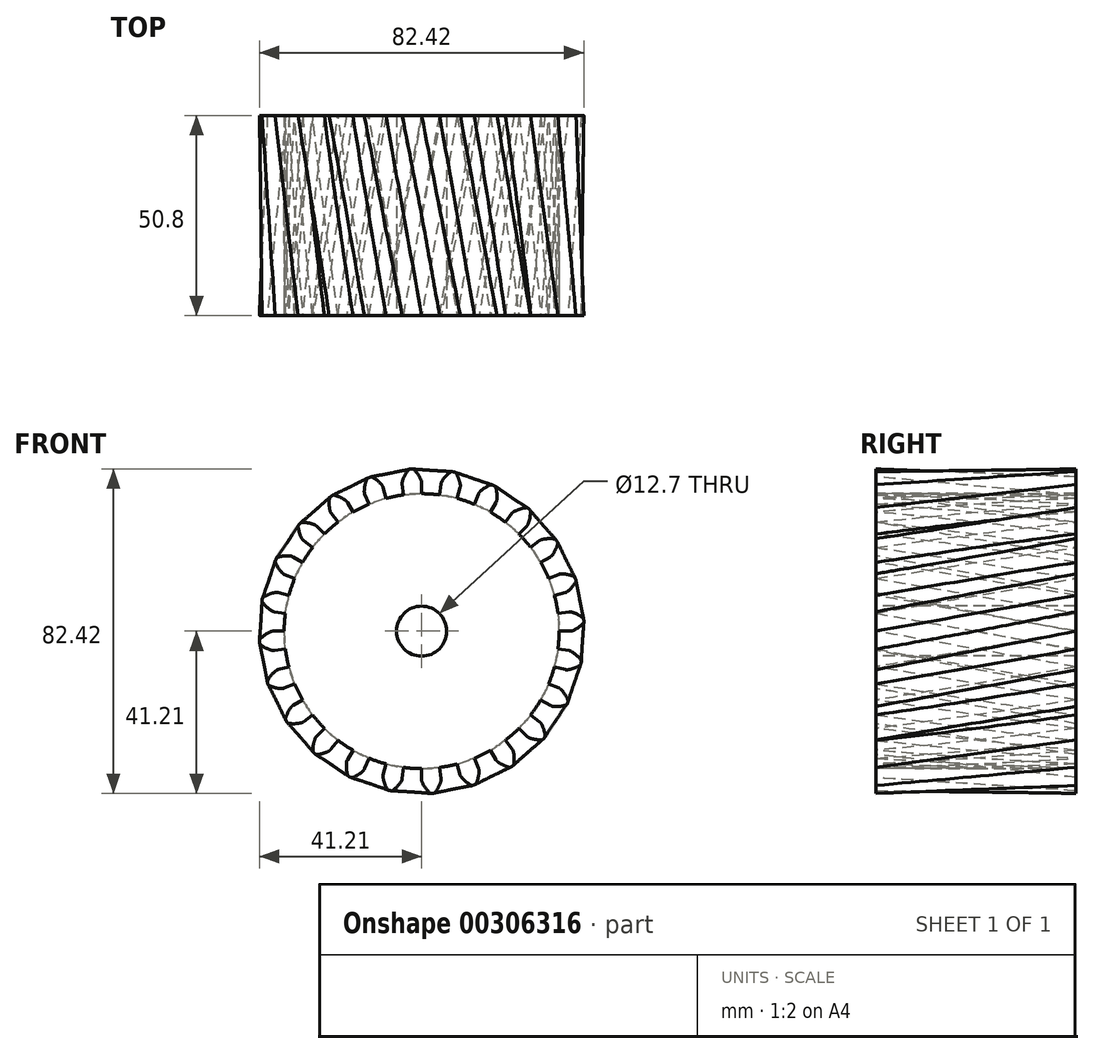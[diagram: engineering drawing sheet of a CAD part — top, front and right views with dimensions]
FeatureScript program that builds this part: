
annotation { "Feature Type Name" : "Feature", "Feature Type Description" : "" }
export const myFeature = defineFeature(function(context is Context, id is Id, definition is map)
    precondition{}
    {
        {
            var Q0;
            Q0=qCreatedBy(makeId("Front.planeOp"),FACE);
            var sketch = newSketch(context, id + "F0", { "sketchPlane" : qUnion([Q0])});
            skCircle(sketch, "E0", {"center": v(0, 0) * mm, "radius": 34.93 * mm});
            skArc(sketch, "E1.trimOffspring", {"start": v(-0.14, 38.43) * mm, "mid": v(-0.94, 39.83) * mm, "end": v(-1.99, 41.06) * mm});
            skLineSegment(sketch, "E2", {"start": v(0, 37.78) * mm, "end": v(0, 34.93) * mm});
            skLineSegment(sketch, "E3", {"start": v(-2.37, 41.2) * mm, "end": v(-2.7, 41.2) * mm});
            skArc(sketch, "E4.MirrorCS", {"start": v(-4.88, 38.12) * mm, "mid": v(-4.27, 39.62) * mm, "end": v(-3.4, 40.97) * mm});
            skLineSegment(sketch, "E5.MirrorCS", {"start": v(-3.03, 41.16) * mm, "end": v(-2.7, 41.2) * mm});
            skLineSegment(sketch, "E6.MirrorCS", {"start": v(-4.93, 37.45) * mm, "end": v(-4.56, 34.63) * mm});
            skPoint(sketch, "E7.visualSharp", {"position": v(-4.97, 37.77) * mm});
            skArc(sketch, "E7.filletArc", {"start": v(-4.88, 38.12) * mm, "mid": v(-4.94, 37.79) * mm, "end": v(-4.93, 37.45) * mm});
            skPoint(sketch, "E8.visualSharp", {"position": v(0, 38.1) * mm});
            skArc(sketch, "E8.filletArc", {"start": v(0, 37.78) * mm, "mid": v(-0.04, 38.11) * mm, "end": v(-0.14, 38.43) * mm});
            skPoint(sketch, "E9.visualSharp", {"position": v(-3.25, 41.15) * mm});
            skArc(sketch, "E9.filletArc", {"start": v(-3.03, 41.16) * mm, "mid": v(-3.23, 41.1) * mm, "end": v(-3.4, 40.97) * mm});
            skPoint(sketch, "E10.visualSharp", {"position": v(-2.15, 41.22) * mm});
            skArc(sketch, "E10.filletArc", {"start": v(-1.99, 41.06) * mm, "mid": v(-2.16, 41.18) * mm, "end": v(-2.37, 41.2) * mm});
            skLineSegment(sketch, "E11.1.0", {"start": v(-14.46, 34.9) * mm, "end": v(-13.37, 32.27) * mm});
            skArc(sketch, "E11.1.1", {"start": v(-14.58, 35.56) * mm, "mid": v(-14.55, 35.22) * mm, "end": v(-14.46, 34.9) * mm});
            skArc(sketch, "E11.1.2", {"start": v(-14.58, 35.56) * mm, "mid": v(-14.38, 37.16) * mm, "end": v(-13.88, 38.7) * mm});
            skLineSegment(sketch, "E11.1.3", {"start": v(-13.58, 38.98) * mm, "end": v(-13.27, 39.09) * mm});
            skLineSegment(sketch, "E11.1.4", {"start": v(-12.95, 39.2) * mm, "end": v(-13.27, 39.09) * mm});
            skArc(sketch, "E11.1.5", {"start": v(-10.08, 37.08) * mm, "mid": v(-11.22, 38.23) * mm, "end": v(-12.55, 39.15) * mm});
            skArc(sketch, "E11.1.6", {"start": v(-9.78, 36.5) * mm, "mid": v(-9.9, 36.8) * mm, "end": v(-10.08, 37.08) * mm});
            skLineSegment(sketch, "E11.1.7", {"start": v(-9.78, 36.5) * mm, "end": v(-9.04, 33.73) * mm});
            skArc(sketch, "E11.1.8", {"start": v(-13.58, 38.98) * mm, "mid": v(-13.76, 38.87) * mm, "end": v(-13.88, 38.7) * mm});
            skArc(sketch, "E11.1.9", {"start": v(-12.55, 39.15) * mm, "mid": v(-12.74, 39.21) * mm, "end": v(-12.95, 39.2) * mm});
            skLineSegment(sketch, "E11.2.0", {"start": v(-23, 29.97) * mm, "end": v(-21.26, 27.7) * mm});
            skArc(sketch, "E11.2.1", {"start": v(-23.28, 30.57) * mm, "mid": v(-23.17, 30.26) * mm, "end": v(-23, 29.97) * mm});
            skArc(sketch, "E11.2.2", {"start": v(-23.28, 30.57) * mm, "mid": v(-23.5, 32.17) * mm, "end": v(-23.42, 33.79) * mm});
            skLineSegment(sketch, "E11.2.3", {"start": v(-23.2, 34.13) * mm, "end": v(-22.93, 34.32) * mm});
            skLineSegment(sketch, "E11.2.4", {"start": v(-22.65, 34.5) * mm, "end": v(-22.93, 34.32) * mm});
            skArc(sketch, "E11.2.5", {"start": v(-19.34, 33.21) * mm, "mid": v(-20.73, 34.03) * mm, "end": v(-22.25, 34.57) * mm});
            skArc(sketch, "E11.2.6", {"start": v(-18.89, 32.72) * mm, "mid": v(-19.09, 32.99) * mm, "end": v(-19.34, 33.21) * mm});
            skLineSegment(sketch, "E11.2.7", {"start": v(-18.89, 32.72) * mm, "end": v(-17.46, 30.25) * mm});
            skArc(sketch, "E11.2.8", {"start": v(-23.2, 34.13) * mm, "mid": v(-23.35, 33.98) * mm, "end": v(-23.42, 33.79) * mm});
            skArc(sketch, "E11.2.9", {"start": v(-22.25, 34.57) * mm, "mid": v(-22.46, 34.58) * mm, "end": v(-22.65, 34.5) * mm});
            skLineSegment(sketch, "E12.2.3.0", {"start": v(-29.97, 23) * mm, "end": v(-27.7, 21.26) * mm});
            skArc(sketch, "E12.3.3.0", {"start": v(-30.4, 23.5) * mm, "mid": v(-30.21, 23.23) * mm, "end": v(-29.97, 23) * mm});
            skArc(sketch, "E12.7.3.0", {"start": v(-30.4, 23.5) * mm, "mid": v(-31.03, 25) * mm, "end": v(-31.37, 26.57) * mm});
            skLineSegment(sketch, "E12.11.3.0", {"start": v(-31.25, 26.96) * mm, "end": v(-31.03, 27.22) * mm});
            skLineSegment(sketch, "E12.14.3.0", {"start": v(-30.81, 27.47) * mm, "end": v(-31.03, 27.22) * mm});
            skArc(sketch, "E12.17.3.0", {"start": v(-27.27, 27.07) * mm, "mid": v(-28.83, 27.5) * mm, "end": v(-30.44, 27.63) * mm});
            skArc(sketch, "E12.21.3.0", {"start": v(-26.71, 26.71) * mm, "mid": v(-26.97, 26.92) * mm, "end": v(-27.27, 27.07) * mm});
            skLineSegment(sketch, "E12.25.3.0", {"start": v(-26.71, 26.71) * mm, "end": v(-24.7, 24.7) * mm});
            skArc(sketch, "E12.28.3.0", {"start": v(-31.25, 26.96) * mm, "mid": v(-31.35, 26.78) * mm, "end": v(-31.37, 26.57) * mm});
            skArc(sketch, "E12.32.3.0", {"start": v(-30.44, 27.63) * mm, "mid": v(-30.64, 27.59) * mm, "end": v(-30.81, 27.47) * mm});
            skLineSegment(sketch, "E12.2.4.0", {"start": v(-34.9, 14.46) * mm, "end": v(-32.27, 13.37) * mm});
            skArc(sketch, "E12.3.4.0", {"start": v(-35.45, 14.84) * mm, "mid": v(-35.2, 14.62) * mm, "end": v(-34.9, 14.46) * mm});
            skArc(sketch, "E12.7.4.0", {"start": v(-35.45, 14.84) * mm, "mid": v(-36.44, 16.11) * mm, "end": v(-37.18, 17.55) * mm});
            skLineSegment(sketch, "E12.11.4.0", {"start": v(-37.17, 17.96) * mm, "end": v(-37.02, 18.26) * mm});
            skLineSegment(sketch, "E12.14.4.0", {"start": v(-36.87, 18.55) * mm, "end": v(-37.02, 18.26) * mm});
            skArc(sketch, "E12.17.4.0", {"start": v(-33.35, 19.1) * mm, "mid": v(-34.97, 19.1) * mm, "end": v(-36.56, 18.81) * mm});
            skArc(sketch, "E12.21.4.0", {"start": v(-32.72, 18.89) * mm, "mid": v(-33.02, 19.02) * mm, "end": v(-33.35, 19.1) * mm});
            skLineSegment(sketch, "E12.25.4.0", {"start": v(-32.72, 18.89) * mm, "end": v(-30.25, 17.46) * mm});
            skArc(sketch, "E12.28.4.0", {"start": v(-37.17, 17.96) * mm, "mid": v(-37.21, 17.75) * mm, "end": v(-37.18, 17.55) * mm});
            skArc(sketch, "E12.32.4.0", {"start": v(-36.56, 18.81) * mm, "mid": v(-36.74, 18.72) * mm, "end": v(-36.87, 18.55) * mm});
            skLineSegment(sketch, "E12.2.5.0", {"start": v(-37.45, 4.93) * mm, "end": v(-34.63, 4.56) * mm});
            skArc(sketch, "E12.3.5.0", {"start": v(-38.08, 5.15) * mm, "mid": v(-37.78, 5) * mm, "end": v(-37.45, 4.93) * mm});
            skArc(sketch, "E12.7.5.0", {"start": v(-38.08, 5.15) * mm, "mid": v(-39.37, 6.13) * mm, "end": v(-40.45, 7.33) * mm});
            skLineSegment(sketch, "E12.11.5.0", {"start": v(-40.55, 7.72) * mm, "end": v(-40.49, 8.05) * mm});
            skLineSegment(sketch, "E12.14.5.0", {"start": v(-40.42, 8.38) * mm, "end": v(-40.49, 8.05) * mm});
            skArc(sketch, "E12.17.5.0", {"start": v(-37.16, 9.81) * mm, "mid": v(-38.72, 9.4) * mm, "end": v(-40.18, 8.71) * mm});
            skArc(sketch, "E12.21.5.0", {"start": v(-36.5, 9.78) * mm, "mid": v(-36.82, 9.83) * mm, "end": v(-37.16, 9.81) * mm});
            skLineSegment(sketch, "E12.25.5.0", {"start": v(-36.5, 9.78) * mm, "end": v(-33.73, 9.04) * mm});
            skArc(sketch, "E12.28.5.0", {"start": v(-40.55, 7.72) * mm, "mid": v(-40.54, 7.52) * mm, "end": v(-40.45, 7.33) * mm});
            skArc(sketch, "E12.32.5.0", {"start": v(-40.18, 8.71) * mm, "mid": v(-40.33, 8.57) * mm, "end": v(-40.42, 8.38) * mm});
            skLineSegment(sketch, "E12.2.6.0", {"start": v(-37.45, -4.93) * mm, "end": v(-34.63, -4.56) * mm});
            skArc(sketch, "E12.3.6.0", {"start": v(-38.12, -4.88) * mm, "mid": v(-37.79, -4.94) * mm, "end": v(-37.45, -4.93) * mm});
            skArc(sketch, "E12.7.6.0", {"start": v(-38.12, -4.88) * mm, "mid": v(-39.62, -4.27) * mm, "end": v(-40.97, -3.4) * mm});
            skLineSegment(sketch, "E12.11.6.0", {"start": v(-41.16, -3.03) * mm, "end": v(-41.2, -2.7) * mm});
            skLineSegment(sketch, "E12.14.6.0", {"start": v(-41.2, -2.37) * mm, "end": v(-41.2, -2.7) * mm});
            skArc(sketch, "E12.17.6.0", {"start": v(-38.43, -0.14) * mm, "mid": v(-39.83, -0.94) * mm, "end": v(-41.06, -1.99) * mm});
            skArc(sketch, "E12.21.6.0", {"start": v(-37.78, 0) * mm, "mid": v(-38.11, -0.04) * mm, "end": v(-38.43, -0.14) * mm});
            skLineSegment(sketch, "E12.25.6.0", {"start": v(-37.78, 0) * mm, "end": v(-34.93, 0) * mm});
            skArc(sketch, "E12.28.6.0", {"start": v(-41.16, -3.03) * mm, "mid": v(-41.1, -3.23) * mm, "end": v(-40.97, -3.4) * mm});
            skArc(sketch, "E12.32.6.0", {"start": v(-41.06, -1.99) * mm, "mid": v(-41.18, -2.16) * mm, "end": v(-41.2, -2.37) * mm});
            skLineSegment(sketch, "E12.2.7.0", {"start": v(-34.9, -14.46) * mm, "end": v(-32.27, -13.37) * mm});
            skArc(sketch, "E12.3.7.0", {"start": v(-35.56, -14.58) * mm, "mid": v(-35.22, -14.55) * mm, "end": v(-34.9, -14.46) * mm});
            skArc(sketch, "E12.7.7.0", {"start": v(-35.56, -14.58) * mm, "mid": v(-37.16, -14.38) * mm, "end": v(-38.7, -13.88) * mm});
            skLineSegment(sketch, "E12.11.7.0", {"start": v(-38.98, -13.58) * mm, "end": v(-39.09, -13.27) * mm});
            skLineSegment(sketch, "E12.14.7.0", {"start": v(-39.2, -12.95) * mm, "end": v(-39.09, -13.27) * mm});
            skArc(sketch, "E12.17.7.0", {"start": v(-37.08, -10.08) * mm, "mid": v(-38.23, -11.22) * mm, "end": v(-39.15, -12.55) * mm});
            skArc(sketch, "E12.21.7.0", {"start": v(-36.5, -9.78) * mm, "mid": v(-36.8, -9.9) * mm, "end": v(-37.08, -10.08) * mm});
            skLineSegment(sketch, "E12.25.7.0", {"start": v(-36.5, -9.78) * mm, "end": v(-33.73, -9.04) * mm});
            skArc(sketch, "E12.28.7.0", {"start": v(-38.98, -13.58) * mm, "mid": v(-38.87, -13.76) * mm, "end": v(-38.7, -13.88) * mm});
            skArc(sketch, "E12.32.7.0", {"start": v(-39.15, -12.55) * mm, "mid": v(-39.21, -12.74) * mm, "end": v(-39.2, -12.95) * mm});
            skLineSegment(sketch, "E12.2.8.0", {"start": v(-29.97, -23) * mm, "end": v(-27.7, -21.26) * mm});
            skArc(sketch, "E12.3.8.0", {"start": v(-30.57, -23.28) * mm, "mid": v(-30.26, -23.17) * mm, "end": v(-29.97, -23) * mm});
            skArc(sketch, "E12.7.8.0", {"start": v(-30.57, -23.28) * mm, "mid": v(-32.17, -23.5) * mm, "end": v(-33.79, -23.42) * mm});
            skLineSegment(sketch, "E12.11.8.0", {"start": v(-34.13, -23.2) * mm, "end": v(-34.32, -22.93) * mm});
            skLineSegment(sketch, "E12.14.8.0", {"start": v(-34.5, -22.65) * mm, "end": v(-34.32, -22.93) * mm});
            skArc(sketch, "E12.17.8.0", {"start": v(-33.21, -19.34) * mm, "mid": v(-34.03, -20.73) * mm, "end": v(-34.57, -22.25) * mm});
            skArc(sketch, "E12.21.8.0", {"start": v(-32.72, -18.89) * mm, "mid": v(-32.99, -19.09) * mm, "end": v(-33.21, -19.34) * mm});
            skLineSegment(sketch, "E12.25.8.0", {"start": v(-32.72, -18.89) * mm, "end": v(-30.25, -17.46) * mm});
            skArc(sketch, "E12.28.8.0", {"start": v(-34.13, -23.2) * mm, "mid": v(-33.98, -23.35) * mm, "end": v(-33.79, -23.42) * mm});
            skArc(sketch, "E12.32.8.0", {"start": v(-34.57, -22.25) * mm, "mid": v(-34.58, -22.46) * mm, "end": v(-34.5, -22.65) * mm});
            skLineSegment(sketch, "E12.2.9.0", {"start": v(-23, -29.97) * mm, "end": v(-21.26, -27.7) * mm});
            skArc(sketch, "E12.3.9.0", {"start": v(-23.5, -30.4) * mm, "mid": v(-23.23, -30.21) * mm, "end": v(-23, -29.97) * mm});
            skArc(sketch, "E12.7.9.0", {"start": v(-23.5, -30.4) * mm, "mid": v(-25, -31.03) * mm, "end": v(-26.57, -31.37) * mm});
            skLineSegment(sketch, "E12.11.9.0", {"start": v(-26.96, -31.25) * mm, "end": v(-27.22, -31.03) * mm});
            skLineSegment(sketch, "E12.14.9.0", {"start": v(-27.47, -30.81) * mm, "end": v(-27.22, -31.03) * mm});
            skArc(sketch, "E12.17.9.0", {"start": v(-27.07, -27.27) * mm, "mid": v(-27.5, -28.83) * mm, "end": v(-27.63, -30.44) * mm});
            skArc(sketch, "E12.21.9.0", {"start": v(-26.71, -26.71) * mm, "mid": v(-26.92, -26.97) * mm, "end": v(-27.07, -27.27) * mm});
            skLineSegment(sketch, "E12.25.9.0", {"start": v(-26.71, -26.71) * mm, "end": v(-24.7, -24.7) * mm});
            skArc(sketch, "E12.28.9.0", {"start": v(-26.96, -31.25) * mm, "mid": v(-26.78, -31.35) * mm, "end": v(-26.57, -31.37) * mm});
            skArc(sketch, "E12.32.9.0", {"start": v(-27.63, -30.44) * mm, "mid": v(-27.59, -30.64) * mm, "end": v(-27.47, -30.81) * mm});
            skLineSegment(sketch, "E12.2.10.0", {"start": v(-14.46, -34.9) * mm, "end": v(-13.37, -32.27) * mm});
            skArc(sketch, "E12.3.10.0", {"start": v(-14.84, -35.45) * mm, "mid": v(-14.62, -35.2) * mm, "end": v(-14.46, -34.9) * mm});
            skArc(sketch, "E12.7.10.0", {"start": v(-14.84, -35.45) * mm, "mid": v(-16.11, -36.44) * mm, "end": v(-17.55, -37.18) * mm});
            skLineSegment(sketch, "E12.11.10.0", {"start": v(-17.96, -37.17) * mm, "end": v(-18.26, -37.02) * mm});
            skLineSegment(sketch, "E12.14.10.0", {"start": v(-18.55, -36.87) * mm, "end": v(-18.26, -37.02) * mm});
            skArc(sketch, "E12.17.10.0", {"start": v(-19.1, -33.35) * mm, "mid": v(-19.1, -34.97) * mm, "end": v(-18.81, -36.56) * mm});
            skArc(sketch, "E12.21.10.0", {"start": v(-18.89, -32.72) * mm, "mid": v(-19.02, -33.02) * mm, "end": v(-19.1, -33.35) * mm});
            skLineSegment(sketch, "E12.25.10.0", {"start": v(-18.89, -32.72) * mm, "end": v(-17.46, -30.25) * mm});
            skArc(sketch, "E12.28.10.0", {"start": v(-17.96, -37.17) * mm, "mid": v(-17.75, -37.21) * mm, "end": v(-17.55, -37.18) * mm});
            skArc(sketch, "E12.32.10.0", {"start": v(-18.81, -36.56) * mm, "mid": v(-18.72, -36.74) * mm, "end": v(-18.55, -36.87) * mm});
            skLineSegment(sketch, "E12.2.11.0", {"start": v(-4.93, -37.45) * mm, "end": v(-4.56, -34.63) * mm});
            skArc(sketch, "E12.3.11.0", {"start": v(-5.15, -38.08) * mm, "mid": v(-5, -37.78) * mm, "end": v(-4.93, -37.45) * mm});
            skArc(sketch, "E12.7.11.0", {"start": v(-5.15, -38.08) * mm, "mid": v(-6.13, -39.37) * mm, "end": v(-7.33, -40.45) * mm});
            skLineSegment(sketch, "E12.11.11.0", {"start": v(-7.72, -40.55) * mm, "end": v(-8.05, -40.49) * mm});
            skLineSegment(sketch, "E12.14.11.0", {"start": v(-8.38, -40.42) * mm, "end": v(-8.05, -40.49) * mm});
            skArc(sketch, "E12.17.11.0", {"start": v(-9.81, -37.16) * mm, "mid": v(-9.4, -38.72) * mm, "end": v(-8.71, -40.18) * mm});
            skArc(sketch, "E12.21.11.0", {"start": v(-9.78, -36.5) * mm, "mid": v(-9.83, -36.82) * mm, "end": v(-9.81, -37.16) * mm});
            skLineSegment(sketch, "E12.25.11.0", {"start": v(-9.78, -36.5) * mm, "end": v(-9.04, -33.73) * mm});
            skArc(sketch, "E12.28.11.0", {"start": v(-7.72, -40.55) * mm, "mid": v(-7.52, -40.54) * mm, "end": v(-7.33, -40.45) * mm});
            skArc(sketch, "E12.32.11.0", {"start": v(-8.71, -40.18) * mm, "mid": v(-8.57, -40.33) * mm, "end": v(-8.38, -40.42) * mm});
            skLineSegment(sketch, "E12.2.12.0", {"start": v(4.93, -37.45) * mm, "end": v(4.56, -34.63) * mm});
            skArc(sketch, "E12.3.12.0", {"start": v(4.88, -38.12) * mm, "mid": v(4.94, -37.79) * mm, "end": v(4.93, -37.45) * mm});
            skArc(sketch, "E12.7.12.0", {"start": v(4.88, -38.12) * mm, "mid": v(4.27, -39.62) * mm, "end": v(3.4, -40.97) * mm});
            skLineSegment(sketch, "E12.11.12.0", {"start": v(3.03, -41.16) * mm, "end": v(2.7, -41.2) * mm});
            skLineSegment(sketch, "E12.14.12.0", {"start": v(2.37, -41.2) * mm, "end": v(2.7, -41.2) * mm});
            skArc(sketch, "E12.17.12.0", {"start": v(0.14, -38.43) * mm, "mid": v(0.94, -39.83) * mm, "end": v(1.99, -41.06) * mm});
            skArc(sketch, "E12.21.12.0", {"start": v(0, -37.78) * mm, "mid": v(0.04, -38.11) * mm, "end": v(0.14, -38.43) * mm});
            skLineSegment(sketch, "E12.25.12.0", {"start": v(0, -37.78) * mm, "end": v(0, -34.93) * mm});
            skArc(sketch, "E12.28.12.0", {"start": v(3.03, -41.16) * mm, "mid": v(3.23, -41.1) * mm, "end": v(3.4, -40.97) * mm});
            skArc(sketch, "E12.32.12.0", {"start": v(1.99, -41.06) * mm, "mid": v(2.16, -41.18) * mm, "end": v(2.37, -41.2) * mm});
            skLineSegment(sketch, "E12.2.13.0", {"start": v(14.46, -34.9) * mm, "end": v(13.37, -32.27) * mm});
            skArc(sketch, "E12.3.13.0", {"start": v(14.58, -35.56) * mm, "mid": v(14.55, -35.22) * mm, "end": v(14.46, -34.9) * mm});
            skArc(sketch, "E12.7.13.0", {"start": v(14.58, -35.56) * mm, "mid": v(14.38, -37.16) * mm, "end": v(13.88, -38.7) * mm});
            skLineSegment(sketch, "E12.11.13.0", {"start": v(13.58, -38.98) * mm, "end": v(13.27, -39.09) * mm});
            skLineSegment(sketch, "E12.14.13.0", {"start": v(12.95, -39.2) * mm, "end": v(13.27, -39.09) * mm});
            skArc(sketch, "E12.17.13.0", {"start": v(10.08, -37.08) * mm, "mid": v(11.22, -38.23) * mm, "end": v(12.55, -39.15) * mm});
            skArc(sketch, "E12.21.13.0", {"start": v(9.78, -36.5) * mm, "mid": v(9.9, -36.8) * mm, "end": v(10.08, -37.08) * mm});
            skLineSegment(sketch, "E12.25.13.0", {"start": v(9.78, -36.5) * mm, "end": v(9.04, -33.73) * mm});
            skArc(sketch, "E12.28.13.0", {"start": v(13.58, -38.98) * mm, "mid": v(13.76, -38.87) * mm, "end": v(13.88, -38.7) * mm});
            skArc(sketch, "E12.32.13.0", {"start": v(12.55, -39.15) * mm, "mid": v(12.74, -39.21) * mm, "end": v(12.95, -39.2) * mm});
            skLineSegment(sketch, "E12.2.14.0", {"start": v(23, -29.97) * mm, "end": v(21.26, -27.7) * mm});
            skArc(sketch, "E12.3.14.0", {"start": v(23.28, -30.57) * mm, "mid": v(23.17, -30.26) * mm, "end": v(23, -29.97) * mm});
            skArc(sketch, "E12.7.14.0", {"start": v(23.28, -30.57) * mm, "mid": v(23.5, -32.17) * mm, "end": v(23.42, -33.79) * mm});
            skLineSegment(sketch, "E12.11.14.0", {"start": v(23.2, -34.13) * mm, "end": v(22.93, -34.32) * mm});
            skLineSegment(sketch, "E12.14.14.0", {"start": v(22.65, -34.5) * mm, "end": v(22.93, -34.32) * mm});
            skArc(sketch, "E12.17.14.0", {"start": v(19.34, -33.21) * mm, "mid": v(20.73, -34.03) * mm, "end": v(22.25, -34.57) * mm});
            skArc(sketch, "E12.21.14.0", {"start": v(18.89, -32.72) * mm, "mid": v(19.09, -32.99) * mm, "end": v(19.34, -33.21) * mm});
            skLineSegment(sketch, "E12.25.14.0", {"start": v(18.89, -32.72) * mm, "end": v(17.46, -30.25) * mm});
            skArc(sketch, "E12.28.14.0", {"start": v(23.2, -34.13) * mm, "mid": v(23.35, -33.98) * mm, "end": v(23.42, -33.79) * mm});
            skArc(sketch, "E12.32.14.0", {"start": v(22.25, -34.57) * mm, "mid": v(22.46, -34.58) * mm, "end": v(22.65, -34.5) * mm});
            skLineSegment(sketch, "E12.2.15.0", {"start": v(29.97, -23) * mm, "end": v(27.7, -21.26) * mm});
            skArc(sketch, "E12.3.15.0", {"start": v(30.4, -23.5) * mm, "mid": v(30.21, -23.23) * mm, "end": v(29.97, -23) * mm});
            skArc(sketch, "E12.7.15.0", {"start": v(30.4, -23.5) * mm, "mid": v(31.03, -25) * mm, "end": v(31.37, -26.57) * mm});
            skLineSegment(sketch, "E12.11.15.0", {"start": v(31.25, -26.96) * mm, "end": v(31.03, -27.22) * mm});
            skLineSegment(sketch, "E12.14.15.0", {"start": v(30.81, -27.47) * mm, "end": v(31.03, -27.22) * mm});
            skArc(sketch, "E12.17.15.0", {"start": v(27.27, -27.07) * mm, "mid": v(28.83, -27.5) * mm, "end": v(30.44, -27.63) * mm});
            skArc(sketch, "E12.21.15.0", {"start": v(26.71, -26.71) * mm, "mid": v(26.97, -26.92) * mm, "end": v(27.27, -27.07) * mm});
            skLineSegment(sketch, "E12.25.15.0", {"start": v(26.71, -26.71) * mm, "end": v(24.7, -24.7) * mm});
            skArc(sketch, "E12.28.15.0", {"start": v(31.25, -26.96) * mm, "mid": v(31.35, -26.78) * mm, "end": v(31.37, -26.57) * mm});
            skArc(sketch, "E12.32.15.0", {"start": v(30.44, -27.63) * mm, "mid": v(30.64, -27.59) * mm, "end": v(30.81, -27.47) * mm});
            skLineSegment(sketch, "E12.2.16.0", {"start": v(34.9, -14.46) * mm, "end": v(32.27, -13.37) * mm});
            skArc(sketch, "E12.3.16.0", {"start": v(35.45, -14.84) * mm, "mid": v(35.2, -14.62) * mm, "end": v(34.9, -14.46) * mm});
            skArc(sketch, "E12.7.16.0", {"start": v(35.45, -14.84) * mm, "mid": v(36.44, -16.11) * mm, "end": v(37.18, -17.55) * mm});
            skLineSegment(sketch, "E12.11.16.0", {"start": v(37.17, -17.96) * mm, "end": v(37.02, -18.26) * mm});
            skLineSegment(sketch, "E12.14.16.0", {"start": v(36.87, -18.55) * mm, "end": v(37.02, -18.26) * mm});
            skArc(sketch, "E12.17.16.0", {"start": v(33.35, -19.1) * mm, "mid": v(34.97, -19.1) * mm, "end": v(36.56, -18.81) * mm});
            skArc(sketch, "E12.21.16.0", {"start": v(32.72, -18.89) * mm, "mid": v(33.02, -19.02) * mm, "end": v(33.35, -19.1) * mm});
            skLineSegment(sketch, "E12.25.16.0", {"start": v(32.72, -18.89) * mm, "end": v(30.25, -17.46) * mm});
            skArc(sketch, "E12.28.16.0", {"start": v(37.17, -17.96) * mm, "mid": v(37.21, -17.75) * mm, "end": v(37.18, -17.55) * mm});
            skArc(sketch, "E12.32.16.0", {"start": v(36.56, -18.81) * mm, "mid": v(36.74, -18.72) * mm, "end": v(36.87, -18.55) * mm});
            skLineSegment(sketch, "E12.2.17.0", {"start": v(37.45, -4.93) * mm, "end": v(34.63, -4.56) * mm});
            skArc(sketch, "E12.3.17.0", {"start": v(38.08, -5.15) * mm, "mid": v(37.78, -5) * mm, "end": v(37.45, -4.93) * mm});
            skArc(sketch, "E12.7.17.0", {"start": v(38.08, -5.15) * mm, "mid": v(39.37, -6.13) * mm, "end": v(40.45, -7.33) * mm});
            skLineSegment(sketch, "E12.11.17.0", {"start": v(40.55, -7.72) * mm, "end": v(40.49, -8.05) * mm});
            skLineSegment(sketch, "E12.14.17.0", {"start": v(40.42, -8.38) * mm, "end": v(40.49, -8.05) * mm});
            skArc(sketch, "E12.17.17.0", {"start": v(37.16, -9.81) * mm, "mid": v(38.72, -9.4) * mm, "end": v(40.18, -8.71) * mm});
            skArc(sketch, "E12.21.17.0", {"start": v(36.5, -9.78) * mm, "mid": v(36.82, -9.83) * mm, "end": v(37.16, -9.81) * mm});
            skLineSegment(sketch, "E12.25.17.0", {"start": v(36.5, -9.78) * mm, "end": v(33.73, -9.04) * mm});
            skArc(sketch, "E12.28.17.0", {"start": v(40.55, -7.72) * mm, "mid": v(40.54, -7.52) * mm, "end": v(40.45, -7.33) * mm});
            skArc(sketch, "E12.32.17.0", {"start": v(40.18, -8.71) * mm, "mid": v(40.33, -8.57) * mm, "end": v(40.42, -8.38) * mm});
            skLineSegment(sketch, "E12.2.18.0", {"start": v(37.45, 4.93) * mm, "end": v(34.63, 4.56) * mm});
            skArc(sketch, "E12.3.18.0", {"start": v(38.12, 4.88) * mm, "mid": v(37.79, 4.94) * mm, "end": v(37.45, 4.93) * mm});
            skArc(sketch, "E12.7.18.0", {"start": v(38.12, 4.88) * mm, "mid": v(39.62, 4.27) * mm, "end": v(40.97, 3.4) * mm});
            skLineSegment(sketch, "E12.11.18.0", {"start": v(41.16, 3.03) * mm, "end": v(41.2, 2.7) * mm});
            skLineSegment(sketch, "E12.14.18.0", {"start": v(41.2, 2.37) * mm, "end": v(41.2, 2.7) * mm});
            skArc(sketch, "E12.17.18.0", {"start": v(38.43, 0.14) * mm, "mid": v(39.83, 0.94) * mm, "end": v(41.06, 1.99) * mm});
            skArc(sketch, "E12.21.18.0", {"start": v(37.78, 0) * mm, "mid": v(38.11, 0.04) * mm, "end": v(38.43, 0.14) * mm});
            skLineSegment(sketch, "E12.25.18.0", {"start": v(37.78, 0) * mm, "end": v(34.93, 0) * mm});
            skArc(sketch, "E12.28.18.0", {"start": v(41.16, 3.03) * mm, "mid": v(41.1, 3.23) * mm, "end": v(40.97, 3.4) * mm});
            skArc(sketch, "E12.32.18.0", {"start": v(41.06, 1.99) * mm, "mid": v(41.18, 2.16) * mm, "end": v(41.2, 2.37) * mm});
            skLineSegment(sketch, "E12.2.19.0", {"start": v(34.9, 14.46) * mm, "end": v(32.27, 13.37) * mm});
            skArc(sketch, "E12.3.19.0", {"start": v(35.56, 14.58) * mm, "mid": v(35.22, 14.55) * mm, "end": v(34.9, 14.46) * mm});
            skArc(sketch, "E12.7.19.0", {"start": v(35.56, 14.58) * mm, "mid": v(37.16, 14.38) * mm, "end": v(38.7, 13.88) * mm});
            skLineSegment(sketch, "E12.11.19.0", {"start": v(38.98, 13.58) * mm, "end": v(39.09, 13.27) * mm});
            skLineSegment(sketch, "E12.14.19.0", {"start": v(39.2, 12.95) * mm, "end": v(39.09, 13.27) * mm});
            skArc(sketch, "E12.17.19.0", {"start": v(37.08, 10.08) * mm, "mid": v(38.23, 11.22) * mm, "end": v(39.15, 12.55) * mm});
            skArc(sketch, "E12.21.19.0", {"start": v(36.5, 9.78) * mm, "mid": v(36.8, 9.9) * mm, "end": v(37.08, 10.08) * mm});
            skLineSegment(sketch, "E12.25.19.0", {"start": v(36.5, 9.78) * mm, "end": v(33.73, 9.04) * mm});
            skArc(sketch, "E12.28.19.0", {"start": v(38.98, 13.58) * mm, "mid": v(38.87, 13.76) * mm, "end": v(38.7, 13.88) * mm});
            skArc(sketch, "E12.32.19.0", {"start": v(39.15, 12.55) * mm, "mid": v(39.21, 12.74) * mm, "end": v(39.2, 12.95) * mm});
            skLineSegment(sketch, "E12.2.20.0", {"start": v(29.97, 23) * mm, "end": v(27.7, 21.26) * mm});
            skArc(sketch, "E12.3.20.0", {"start": v(30.57, 23.28) * mm, "mid": v(30.26, 23.17) * mm, "end": v(29.97, 23) * mm});
            skArc(sketch, "E12.7.20.0", {"start": v(30.57, 23.28) * mm, "mid": v(32.17, 23.5) * mm, "end": v(33.79, 23.42) * mm});
            skLineSegment(sketch, "E12.11.20.0", {"start": v(34.13, 23.2) * mm, "end": v(34.32, 22.93) * mm});
            skLineSegment(sketch, "E12.14.20.0", {"start": v(34.5, 22.65) * mm, "end": v(34.32, 22.93) * mm});
            skArc(sketch, "E12.17.20.0", {"start": v(33.21, 19.34) * mm, "mid": v(34.03, 20.73) * mm, "end": v(34.57, 22.25) * mm});
            skArc(sketch, "E12.21.20.0", {"start": v(32.72, 18.89) * mm, "mid": v(32.99, 19.09) * mm, "end": v(33.21, 19.34) * mm});
            skLineSegment(sketch, "E12.25.20.0", {"start": v(32.72, 18.89) * mm, "end": v(30.25, 17.46) * mm});
            skArc(sketch, "E12.28.20.0", {"start": v(34.13, 23.2) * mm, "mid": v(33.98, 23.35) * mm, "end": v(33.79, 23.42) * mm});
            skArc(sketch, "E12.32.20.0", {"start": v(34.57, 22.25) * mm, "mid": v(34.58, 22.46) * mm, "end": v(34.5, 22.65) * mm});
            skLineSegment(sketch, "E12.2.21.0", {"start": v(23, 29.97) * mm, "end": v(21.26, 27.7) * mm});
            skArc(sketch, "E12.3.21.0", {"start": v(23.5, 30.4) * mm, "mid": v(23.23, 30.21) * mm, "end": v(23, 29.97) * mm});
            skArc(sketch, "E12.7.21.0", {"start": v(23.5, 30.4) * mm, "mid": v(25, 31.03) * mm, "end": v(26.57, 31.37) * mm});
            skLineSegment(sketch, "E12.11.21.0", {"start": v(26.96, 31.25) * mm, "end": v(27.22, 31.03) * mm});
            skLineSegment(sketch, "E12.14.21.0", {"start": v(27.47, 30.81) * mm, "end": v(27.22, 31.03) * mm});
            skArc(sketch, "E12.17.21.0", {"start": v(27.07, 27.27) * mm, "mid": v(27.5, 28.83) * mm, "end": v(27.63, 30.44) * mm});
            skArc(sketch, "E12.21.21.0", {"start": v(26.71, 26.71) * mm, "mid": v(26.92, 26.97) * mm, "end": v(27.07, 27.27) * mm});
            skLineSegment(sketch, "E12.25.21.0", {"start": v(26.71, 26.71) * mm, "end": v(24.7, 24.7) * mm});
            skArc(sketch, "E12.28.21.0", {"start": v(26.96, 31.25) * mm, "mid": v(26.78, 31.35) * mm, "end": v(26.57, 31.37) * mm});
            skArc(sketch, "E12.32.21.0", {"start": v(27.63, 30.44) * mm, "mid": v(27.59, 30.64) * mm, "end": v(27.47, 30.81) * mm});
            skLineSegment(sketch, "E12.2.22.0", {"start": v(14.46, 34.9) * mm, "end": v(13.37, 32.27) * mm});
            skArc(sketch, "E12.3.22.0", {"start": v(14.84, 35.45) * mm, "mid": v(14.62, 35.2) * mm, "end": v(14.46, 34.9) * mm});
            skArc(sketch, "E12.7.22.0", {"start": v(14.84, 35.45) * mm, "mid": v(16.11, 36.44) * mm, "end": v(17.55, 37.18) * mm});
            skLineSegment(sketch, "E12.11.22.0", {"start": v(17.96, 37.17) * mm, "end": v(18.26, 37.02) * mm});
            skLineSegment(sketch, "E12.14.22.0", {"start": v(18.55, 36.87) * mm, "end": v(18.26, 37.02) * mm});
            skArc(sketch, "E12.17.22.0", {"start": v(19.1, 33.35) * mm, "mid": v(19.1, 34.97) * mm, "end": v(18.81, 36.56) * mm});
            skArc(sketch, "E12.21.22.0", {"start": v(18.89, 32.72) * mm, "mid": v(19.02, 33.02) * mm, "end": v(19.1, 33.35) * mm});
            skLineSegment(sketch, "E12.25.22.0", {"start": v(18.89, 32.72) * mm, "end": v(17.46, 30.25) * mm});
            skArc(sketch, "E12.28.22.0", {"start": v(17.96, 37.17) * mm, "mid": v(17.75, 37.21) * mm, "end": v(17.55, 37.18) * mm});
            skArc(sketch, "E12.32.22.0", {"start": v(18.81, 36.56) * mm, "mid": v(18.72, 36.74) * mm, "end": v(18.55, 36.87) * mm});
            skLineSegment(sketch, "E12.2.23.0", {"start": v(4.93, 37.45) * mm, "end": v(4.56, 34.63) * mm});
            skArc(sketch, "E12.3.23.0", {"start": v(5.15, 38.08) * mm, "mid": v(5, 37.78) * mm, "end": v(4.93, 37.45) * mm});
            skArc(sketch, "E12.7.23.0", {"start": v(5.15, 38.08) * mm, "mid": v(6.13, 39.37) * mm, "end": v(7.33, 40.45) * mm});
            skLineSegment(sketch, "E12.11.23.0", {"start": v(7.72, 40.55) * mm, "end": v(8.05, 40.49) * mm});
            skLineSegment(sketch, "E12.14.23.0", {"start": v(8.38, 40.42) * mm, "end": v(8.05, 40.49) * mm});
            skArc(sketch, "E12.17.23.0", {"start": v(9.81, 37.16) * mm, "mid": v(9.4, 38.72) * mm, "end": v(8.71, 40.18) * mm});
            skArc(sketch, "E12.21.23.0", {"start": v(9.78, 36.5) * mm, "mid": v(9.83, 36.82) * mm, "end": v(9.81, 37.16) * mm});
            skLineSegment(sketch, "E12.25.23.0", {"start": v(9.78, 36.5) * mm, "end": v(9.04, 33.73) * mm});
            skArc(sketch, "E12.28.23.0", {"start": v(7.72, 40.55) * mm, "mid": v(7.52, 40.54) * mm, "end": v(7.33, 40.45) * mm});
            skArc(sketch, "E12.32.23.0", {"start": v(8.71, 40.18) * mm, "mid": v(8.57, 40.33) * mm, "end": v(8.38, 40.42) * mm});
            skSolve(sketch);
        }
        {
            var Q0;
            Q0=qCreatedBy(makeId("Front.planeOp"),FACE);
            cPlane(context, id + "F1", {"entities" : qUnion([Q0]), "cplaneType" : CPlaneType.OFFSET, "offset" : 50.8 * mm, "width" : 152.4 * mm, "height" : 152.4 * mm});
        }
        {
            var Q0;
            Q0=qCreatedBy(id+"F1.planeOp",FACE);
            var sketch = newSketch(context, id + "F2", { "sketchPlane" : qUnion([Q0])});
            skArc(sketch, "E13.0.0", {"start": v(34.93, 0) * mm, "mid": v(34.85, 2.28) * mm, "end": v(34.63, 4.56) * mm});
            skArc(sketch, "E13.0.1", {"start": v(34.63, 4.56) * mm, "mid": v(34.25, 6.81) * mm, "end": v(33.73, 9.04) * mm});
            skArc(sketch, "E13.0.2", {"start": v(33.73, 9.04) * mm, "mid": v(33.07, 11.23) * mm, "end": v(32.27, 13.37) * mm});
            skArc(sketch, "E13.0.3", {"start": v(32.27, 13.37) * mm, "mid": v(31.32, 15.45) * mm, "end": v(30.25, 17.46) * mm});
            skArc(sketch, "E13.0.4", {"start": v(30.25, 17.46) * mm, "mid": v(29.04, 19.4) * mm, "end": v(27.7, 21.26) * mm});
            skArc(sketch, "E13.0.5", {"start": v(27.7, 21.26) * mm, "mid": v(26.26, 23.03) * mm, "end": v(24.7, 24.7) * mm});
            skArc(sketch, "E13.0.6", {"start": v(24.7, 24.7) * mm, "mid": v(23.03, 26.26) * mm, "end": v(21.26, 27.7) * mm});
            skArc(sketch, "E13.0.7", {"start": v(21.26, 27.7) * mm, "mid": v(19.4, 29.04) * mm, "end": v(17.46, 30.25) * mm});
            skArc(sketch, "E13.0.8", {"start": v(17.46, 30.25) * mm, "mid": v(15.45, 31.32) * mm, "end": v(13.37, 32.27) * mm});
            skArc(sketch, "E13.0.9", {"start": v(13.37, 32.27) * mm, "mid": v(11.23, 33.07) * mm, "end": v(9.04, 33.73) * mm});
            skArc(sketch, "E13.0.10", {"start": v(9.04, 33.73) * mm, "mid": v(6.81, 34.25) * mm, "end": v(4.56, 34.63) * mm});
            skArc(sketch, "E13.0.11", {"start": v(4.56, 34.63) * mm, "mid": v(2.28, 34.85) * mm, "end": v(0, 34.92) * mm});
            skArc(sketch, "E13.0.12", {"start": v(0, 34.93) * mm, "mid": v(-2.28, 34.85) * mm, "end": v(-4.56, 34.63) * mm});
            skArc(sketch, "E13.0.13", {"start": v(-4.56, 34.63) * mm, "mid": v(-6.81, 34.25) * mm, "end": v(-9.04, 33.73) * mm});
            skArc(sketch, "E13.0.14", {"start": v(-9.04, 33.73) * mm, "mid": v(-11.23, 33.07) * mm, "end": v(-13.37, 32.27) * mm});
            skArc(sketch, "E13.0.15", {"start": v(-13.37, 32.27) * mm, "mid": v(-15.45, 31.32) * mm, "end": v(-17.46, 30.25) * mm});
            skArc(sketch, "E13.0.16", {"start": v(-17.46, 30.25) * mm, "mid": v(-19.4, 29.04) * mm, "end": v(-21.26, 27.7) * mm});
            skArc(sketch, "E13.0.17", {"start": v(-21.26, 27.7) * mm, "mid": v(-23.03, 26.26) * mm, "end": v(-24.7, 24.7) * mm});
            skArc(sketch, "E13.0.18", {"start": v(-24.7, 24.7) * mm, "mid": v(-26.26, 23.03) * mm, "end": v(-27.7, 21.26) * mm});
            skArc(sketch, "E13.0.19", {"start": v(-27.7, 21.26) * mm, "mid": v(-29.04, 19.4) * mm, "end": v(-30.25, 17.46) * mm});
            skArc(sketch, "E13.0.20", {"start": v(-30.25, 17.46) * mm, "mid": v(-31.32, 15.45) * mm, "end": v(-32.27, 13.37) * mm});
            skArc(sketch, "E13.0.21", {"start": v(-32.27, 13.37) * mm, "mid": v(-33.07, 11.23) * mm, "end": v(-33.73, 9.04) * mm});
            skArc(sketch, "E13.0.22", {"start": v(-33.73, 9.04) * mm, "mid": v(-34.25, 6.81) * mm, "end": v(-34.63, 4.56) * mm});
            skArc(sketch, "E13.0.23", {"start": v(-34.63, 4.56) * mm, "mid": v(-34.85, 2.28) * mm, "end": v(-34.92, 0) * mm});
            skArc(sketch, "E13.0.24", {"start": v(-34.93, 0) * mm, "mid": v(-34.85, -2.28) * mm, "end": v(-34.63, -4.56) * mm});
            skArc(sketch, "E13.0.25", {"start": v(-34.63, -4.56) * mm, "mid": v(-34.25, -6.81) * mm, "end": v(-33.73, -9.04) * mm});
            skArc(sketch, "E13.0.26", {"start": v(-33.73, -9.04) * mm, "mid": v(-33.07, -11.23) * mm, "end": v(-32.27, -13.37) * mm});
            skArc(sketch, "E13.0.27", {"start": v(-32.27, -13.37) * mm, "mid": v(-31.32, -15.45) * mm, "end": v(-30.25, -17.46) * mm});
            skArc(sketch, "E13.0.28", {"start": v(-30.25, -17.46) * mm, "mid": v(-29.04, -19.4) * mm, "end": v(-27.7, -21.26) * mm});
            skArc(sketch, "E13.0.29", {"start": v(-27.7, -21.26) * mm, "mid": v(-26.26, -23.03) * mm, "end": v(-24.7, -24.7) * mm});
            skArc(sketch, "E13.0.30", {"start": v(-24.7, -24.7) * mm, "mid": v(-23.03, -26.26) * mm, "end": v(-21.26, -27.7) * mm});
            skArc(sketch, "E13.0.31", {"start": v(-21.26, -27.7) * mm, "mid": v(-19.4, -29.04) * mm, "end": v(-17.46, -30.25) * mm});
            skArc(sketch, "E13.0.32", {"start": v(-17.46, -30.25) * mm, "mid": v(-15.45, -31.32) * mm, "end": v(-13.37, -32.27) * mm});
            skArc(sketch, "E13.0.33", {"start": v(-13.37, -32.27) * mm, "mid": v(-11.23, -33.07) * mm, "end": v(-9.04, -33.73) * mm});
            skArc(sketch, "E13.0.34", {"start": v(-9.04, -33.73) * mm, "mid": v(-6.81, -34.25) * mm, "end": v(-4.56, -34.63) * mm});
            skArc(sketch, "E13.0.35", {"start": v(-4.56, -34.63) * mm, "mid": v(-2.28, -34.85) * mm, "end": v(0, -34.93) * mm});
            skArc(sketch, "E13.0.36", {"start": v(0, -34.93) * mm, "mid": v(2.28, -34.85) * mm, "end": v(4.56, -34.63) * mm});
            skArc(sketch, "E13.0.37", {"start": v(4.56, -34.63) * mm, "mid": v(6.81, -34.25) * mm, "end": v(9.04, -33.73) * mm});
            skArc(sketch, "E13.0.38", {"start": v(9.04, -33.73) * mm, "mid": v(11.23, -33.07) * mm, "end": v(13.37, -32.27) * mm});
            skArc(sketch, "E13.0.39", {"start": v(13.37, -32.27) * mm, "mid": v(15.45, -31.32) * mm, "end": v(17.46, -30.25) * mm});
            skArc(sketch, "E13.0.40", {"start": v(17.46, -30.25) * mm, "mid": v(19.4, -29.04) * mm, "end": v(21.26, -27.7) * mm});
            skArc(sketch, "E13.0.41", {"start": v(21.26, -27.7) * mm, "mid": v(23.03, -26.26) * mm, "end": v(24.7, -24.7) * mm});
            skArc(sketch, "E13.0.42", {"start": v(24.7, -24.7) * mm, "mid": v(26.26, -23.03) * mm, "end": v(27.7, -21.26) * mm});
            skArc(sketch, "E13.0.43", {"start": v(27.7, -21.26) * mm, "mid": v(29.04, -19.4) * mm, "end": v(30.25, -17.46) * mm});
            skArc(sketch, "E13.0.44", {"start": v(30.25, -17.46) * mm, "mid": v(31.32, -15.45) * mm, "end": v(32.27, -13.37) * mm});
            skArc(sketch, "E13.0.45", {"start": v(32.27, -13.37) * mm, "mid": v(33.07, -11.23) * mm, "end": v(33.73, -9.04) * mm});
            skArc(sketch, "E13.0.46", {"start": v(33.73, -9.04) * mm, "mid": v(34.25, -6.81) * mm, "end": v(34.63, -4.56) * mm});
            skArc(sketch, "E13.0.47", {"start": v(34.63, -4.56) * mm, "mid": v(34.85, -2.28) * mm, "end": v(34.93, 0) * mm});
            skArc(sketch, "E14.0.0", {"start": v(-3.4, 40.97) * mm, "mid": v(-4.27, 39.62) * mm, "end": v(-4.88, 38.12) * mm});
            skArc(sketch, "E14.0.1", {"start": v(-4.88, 38.12) * mm, "mid": v(-4.94, 37.79) * mm, "end": v(-4.93, 37.45) * mm});
            skLineSegment(sketch, "E14.0.2", {"start": v(-4.93, 37.45) * mm, "end": v(-4.56, 34.63) * mm});
            skArc(sketch, "E14.0.3", {"start": v(-4.56, 34.63) * mm, "mid": v(-2.28, 34.85) * mm, "end": v(0, 34.93) * mm});
            skLineSegment(sketch, "E14.0.4", {"start": v(0, 34.93) * mm, "end": v(0, 37.78) * mm});
            skArc(sketch, "E14.0.5", {"start": v(0, 37.78) * mm, "mid": v(-0.04, 38.11) * mm, "end": v(-0.14, 38.43) * mm});
            skArc(sketch, "E14.0.6", {"start": v(-0.14, 38.43) * mm, "mid": v(-0.94, 39.83) * mm, "end": v(-1.99, 41.06) * mm});
            skArc(sketch, "E14.0.7", {"start": v(-1.99, 41.06) * mm, "mid": v(-2.16, 41.18) * mm, "end": v(-2.37, 41.2) * mm});
            skLineSegment(sketch, "E14.0.8", {"start": v(-2.37, 41.2) * mm, "end": v(-2.7, 41.2) * mm});
            skLineSegment(sketch, "E14.0.9", {"start": v(-2.7, 41.2) * mm, "end": v(-3.03, 41.16) * mm});
            skArc(sketch, "E14.0.10", {"start": v(-3.03, 41.16) * mm, "mid": v(-3.23, 41.1) * mm, "end": v(-3.4, 40.97) * mm});
            skSolve(sketch);
        }
        {
            var Q0;
            Q0=makeQuery(id+"F2.imprint","IMPRINT",FACE,{"disambiguationData":[TD([[makeQuery(id+"F2.imprint","IMPRINT",EDGE,{"derivedFrom":sQuery(id+"F2.wireOp",EDGE,"E14.0.0")}),1.0]])]});
            var Q1;
            {var subQ1=sQuery(id+"F0.wireOp",EDGE,"E11.1.0");Q1=makeQuery(id+"F0.imprint","IMPRINT",FACE,{"disambiguationData":[TD([[makeQuery(id+"F0.imprint","IMPRINT",EDGE,{"derivedFrom":subQ1}),1.0]])]});}
            loft(context, id + "F3", {"sheetProfilesArray" : [{ "sheetProfileEntities" : qUnion([Q0]) }, { "sheetProfileEntities" : qUnion([Q1]) }]});
        }
        {
            var Q0;
            Q0=qCreatedBy(id+"F1.planeOp",FACE);
            var sketch = newSketch(context, id + "F4", { "sketchPlane" : qUnion([Q0])});
            skCircle(sketch, "E15", {"center": v(0, 0) * mm, "radius": 34.93 * mm});
            skSolve(sketch);
        }
        {
            var Q0;
            Q0 = qSketchRegion(id + "F4", true);
            var Q1;
            {var subQ1=sQuery(id+"F0.wireOp",EDGE,"E11.1.0");Q1=makeQuery(id+"F3.opLoft","CAP_FACE",FACE,{"disambiguationData":[OSD([makeQuery(id+"F0.imprint","IMPRINT",FACE,{"disambiguationData":[TD([[makeQuery(id+"F0.imprint","IMPRINT",EDGE,{"derivedFrom":subQ1}),1.0]])]})])],"isStart":true});}
            extrude(context, id + "F5", {"entities" : qUnion([Q0]), "operationType" : NewBodyOperationType.ADD, "endBound" : BoundingType.UP_TO_SURFACE, "oppositeDirection" : true, "endBoundEntityFace" : qUnion([Q1]), "depth" : 25.4 * mm});
        }
        {
            var Q0;
            {var subQ1=sQuery(id+"F0.wireOp",EDGE,"E11.1.0");Q0=makeQuery(id+"F3.opLoft","SWEPT_BODY",BODY,{"disambiguationData":[OSD([makeQuery(id+"F0.imprint","IMPRINT",FACE,{"disambiguationData":[TD([[makeQuery(id+"F0.imprint","IMPRINT",EDGE,{"derivedFrom":subQ1}),1.0]])]}),makeQuery(id+"F2.imprint","IMPRINT",FACE,{"disambiguationData":[TD([[makeQuery(id+"F2.imprint","IMPRINT",EDGE,{"derivedFrom":sQuery(id+"F2.wireOp",EDGE,"E14.0.0")}),1.0]])]})])]});}
            var Q1;
            Q1=makeQuery(id+"F5.opExtrude","SWEPT_FACE",FACE,{"disambiguationData":[OSD([sQuery(id+"F4.wireOp",EDGE,"E15")])]});
            circularPattern(context, id + "F6", {"entities" : qUnion([Q0]), "axis" : qUnion([Q1]), "angle" : 360 * degree, "instanceCount" : 24, "equalSpace" : true});
        }
        {
            var Q0;
            {var subQ1=sQuery(id+"F0.wireOp",EDGE,"E11.1.0");Q0=makeQuery(id+"F3.opLoft","SWEPT_BODY",BODY,{"disambiguationData":[OSD([makeQuery(id+"F0.imprint","IMPRINT",FACE,{"disambiguationData":[TD([[makeQuery(id+"F0.imprint","IMPRINT",EDGE,{"derivedFrom":subQ1}),1.0]])]}),makeQuery(id+"F2.imprint","IMPRINT",FACE,{"disambiguationData":[TD([[makeQuery(id+"F2.imprint","IMPRINT",EDGE,{"derivedFrom":sQuery(id+"F2.wireOp",EDGE,"E14.0.0")}),1.0]])]})])]});}
            var Q1;
            {var subQ1=sQuery(id+"F0.wireOp",EDGE,"E11.1.0");Q1=makeQuery(id+"F6.opPattern","COPY",BODY,{"derivedFrom":makeQuery(id+"F3.opLoft","SWEPT_BODY",BODY,{"disambiguationData":[OSD([makeQuery(id+"F0.imprint","IMPRINT",FACE,{"disambiguationData":[TD([[makeQuery(id+"F0.imprint","IMPRINT",EDGE,{"derivedFrom":subQ1}),1.0]])]}),makeQuery(id+"F2.imprint","IMPRINT",FACE,{"disambiguationData":[TD([[makeQuery(id+"F2.imprint","IMPRINT",EDGE,{"derivedFrom":sQuery(id+"F2.wireOp",EDGE,"E14.0.0")}),1.0]])]})])]}),"instanceName":"23"});}
            var Q2;
            {var subQ1=sQuery(id+"F0.wireOp",EDGE,"E11.1.0");Q2=makeQuery(id+"F6.opPattern","COPY",BODY,{"derivedFrom":makeQuery(id+"F3.opLoft","SWEPT_BODY",BODY,{"disambiguationData":[OSD([makeQuery(id+"F0.imprint","IMPRINT",FACE,{"disambiguationData":[TD([[makeQuery(id+"F0.imprint","IMPRINT",EDGE,{"derivedFrom":subQ1}),1.0]])]}),makeQuery(id+"F2.imprint","IMPRINT",FACE,{"disambiguationData":[TD([[makeQuery(id+"F2.imprint","IMPRINT",EDGE,{"derivedFrom":sQuery(id+"F2.wireOp",EDGE,"E14.0.0")}),1.0]])]})])]}),"instanceName":"22"});}
            var Q3;
            {var subQ1=sQuery(id+"F0.wireOp",EDGE,"E11.1.0");Q3=makeQuery(id+"F6.opPattern","COPY",BODY,{"derivedFrom":makeQuery(id+"F3.opLoft","SWEPT_BODY",BODY,{"disambiguationData":[OSD([makeQuery(id+"F0.imprint","IMPRINT",FACE,{"disambiguationData":[TD([[makeQuery(id+"F0.imprint","IMPRINT",EDGE,{"derivedFrom":subQ1}),1.0]])]}),makeQuery(id+"F2.imprint","IMPRINT",FACE,{"disambiguationData":[TD([[makeQuery(id+"F2.imprint","IMPRINT",EDGE,{"derivedFrom":sQuery(id+"F2.wireOp",EDGE,"E14.0.0")}),1.0]])]})])]}),"instanceName":"21"});}
            var Q4;
            {var subQ1=sQuery(id+"F0.wireOp",EDGE,"E11.1.0");Q4=makeQuery(id+"F6.opPattern","COPY",BODY,{"derivedFrom":makeQuery(id+"F3.opLoft","SWEPT_BODY",BODY,{"disambiguationData":[OSD([makeQuery(id+"F0.imprint","IMPRINT",FACE,{"disambiguationData":[TD([[makeQuery(id+"F0.imprint","IMPRINT",EDGE,{"derivedFrom":subQ1}),1.0]])]}),makeQuery(id+"F2.imprint","IMPRINT",FACE,{"disambiguationData":[TD([[makeQuery(id+"F2.imprint","IMPRINT",EDGE,{"derivedFrom":sQuery(id+"F2.wireOp",EDGE,"E14.0.0")}),1.0]])]})])]}),"instanceName":"20"});}
            var Q5;
            {var subQ1=sQuery(id+"F0.wireOp",EDGE,"E11.1.0");Q5=makeQuery(id+"F6.opPattern","COPY",BODY,{"derivedFrom":makeQuery(id+"F3.opLoft","SWEPT_BODY",BODY,{"disambiguationData":[OSD([makeQuery(id+"F0.imprint","IMPRINT",FACE,{"disambiguationData":[TD([[makeQuery(id+"F0.imprint","IMPRINT",EDGE,{"derivedFrom":subQ1}),1.0]])]}),makeQuery(id+"F2.imprint","IMPRINT",FACE,{"disambiguationData":[TD([[makeQuery(id+"F2.imprint","IMPRINT",EDGE,{"derivedFrom":sQuery(id+"F2.wireOp",EDGE,"E14.0.0")}),1.0]])]})])]}),"instanceName":"19"});}
            var Q6;
            {var subQ1=sQuery(id+"F0.wireOp",EDGE,"E11.1.0");Q6=makeQuery(id+"F6.opPattern","COPY",BODY,{"derivedFrom":makeQuery(id+"F3.opLoft","SWEPT_BODY",BODY,{"disambiguationData":[OSD([makeQuery(id+"F0.imprint","IMPRINT",FACE,{"disambiguationData":[TD([[makeQuery(id+"F0.imprint","IMPRINT",EDGE,{"derivedFrom":subQ1}),1.0]])]}),makeQuery(id+"F2.imprint","IMPRINT",FACE,{"disambiguationData":[TD([[makeQuery(id+"F2.imprint","IMPRINT",EDGE,{"derivedFrom":sQuery(id+"F2.wireOp",EDGE,"E14.0.0")}),1.0]])]})])]}),"instanceName":"18"});}
            var Q7;
            {var subQ1=sQuery(id+"F0.wireOp",EDGE,"E11.1.0");Q7=makeQuery(id+"F6.opPattern","COPY",BODY,{"derivedFrom":makeQuery(id+"F3.opLoft","SWEPT_BODY",BODY,{"disambiguationData":[OSD([makeQuery(id+"F0.imprint","IMPRINT",FACE,{"disambiguationData":[TD([[makeQuery(id+"F0.imprint","IMPRINT",EDGE,{"derivedFrom":subQ1}),1.0]])]}),makeQuery(id+"F2.imprint","IMPRINT",FACE,{"disambiguationData":[TD([[makeQuery(id+"F2.imprint","IMPRINT",EDGE,{"derivedFrom":sQuery(id+"F2.wireOp",EDGE,"E14.0.0")}),1.0]])]})])]}),"instanceName":"17"});}
            var Q8;
            {var subQ1=sQuery(id+"F0.wireOp",EDGE,"E11.1.0");Q8=makeQuery(id+"F6.opPattern","COPY",BODY,{"derivedFrom":makeQuery(id+"F3.opLoft","SWEPT_BODY",BODY,{"disambiguationData":[OSD([makeQuery(id+"F0.imprint","IMPRINT",FACE,{"disambiguationData":[TD([[makeQuery(id+"F0.imprint","IMPRINT",EDGE,{"derivedFrom":subQ1}),1.0]])]}),makeQuery(id+"F2.imprint","IMPRINT",FACE,{"disambiguationData":[TD([[makeQuery(id+"F2.imprint","IMPRINT",EDGE,{"derivedFrom":sQuery(id+"F2.wireOp",EDGE,"E14.0.0")}),1.0]])]})])]}),"instanceName":"16"});}
            var Q9;
            {var subQ1=sQuery(id+"F0.wireOp",EDGE,"E11.1.0");Q9=makeQuery(id+"F6.opPattern","COPY",BODY,{"derivedFrom":makeQuery(id+"F3.opLoft","SWEPT_BODY",BODY,{"disambiguationData":[OSD([makeQuery(id+"F0.imprint","IMPRINT",FACE,{"disambiguationData":[TD([[makeQuery(id+"F0.imprint","IMPRINT",EDGE,{"derivedFrom":subQ1}),1.0]])]}),makeQuery(id+"F2.imprint","IMPRINT",FACE,{"disambiguationData":[TD([[makeQuery(id+"F2.imprint","IMPRINT",EDGE,{"derivedFrom":sQuery(id+"F2.wireOp",EDGE,"E14.0.0")}),1.0]])]})])]}),"instanceName":"15"});}
            var Q10;
            {var subQ1=sQuery(id+"F0.wireOp",EDGE,"E11.1.0");Q10=makeQuery(id+"F6.opPattern","COPY",BODY,{"derivedFrom":makeQuery(id+"F3.opLoft","SWEPT_BODY",BODY,{"disambiguationData":[OSD([makeQuery(id+"F0.imprint","IMPRINT",FACE,{"disambiguationData":[TD([[makeQuery(id+"F0.imprint","IMPRINT",EDGE,{"derivedFrom":subQ1}),1.0]])]}),makeQuery(id+"F2.imprint","IMPRINT",FACE,{"disambiguationData":[TD([[makeQuery(id+"F2.imprint","IMPRINT",EDGE,{"derivedFrom":sQuery(id+"F2.wireOp",EDGE,"E14.0.0")}),1.0]])]})])]}),"instanceName":"14"});}
            var Q11;
            {var subQ1=sQuery(id+"F0.wireOp",EDGE,"E11.1.0");Q11=makeQuery(id+"F6.opPattern","COPY",BODY,{"derivedFrom":makeQuery(id+"F3.opLoft","SWEPT_BODY",BODY,{"disambiguationData":[OSD([makeQuery(id+"F0.imprint","IMPRINT",FACE,{"disambiguationData":[TD([[makeQuery(id+"F0.imprint","IMPRINT",EDGE,{"derivedFrom":subQ1}),1.0]])]}),makeQuery(id+"F2.imprint","IMPRINT",FACE,{"disambiguationData":[TD([[makeQuery(id+"F2.imprint","IMPRINT",EDGE,{"derivedFrom":sQuery(id+"F2.wireOp",EDGE,"E14.0.0")}),1.0]])]})])]}),"instanceName":"13"});}
            var Q12;
            {var subQ1=sQuery(id+"F0.wireOp",EDGE,"E11.1.0");Q12=makeQuery(id+"F6.opPattern","COPY",BODY,{"derivedFrom":makeQuery(id+"F3.opLoft","SWEPT_BODY",BODY,{"disambiguationData":[OSD([makeQuery(id+"F0.imprint","IMPRINT",FACE,{"disambiguationData":[TD([[makeQuery(id+"F0.imprint","IMPRINT",EDGE,{"derivedFrom":subQ1}),1.0]])]}),makeQuery(id+"F2.imprint","IMPRINT",FACE,{"disambiguationData":[TD([[makeQuery(id+"F2.imprint","IMPRINT",EDGE,{"derivedFrom":sQuery(id+"F2.wireOp",EDGE,"E14.0.0")}),1.0]])]})])]}),"instanceName":"12"});}
            var Q13;
            {var subQ1=sQuery(id+"F0.wireOp",EDGE,"E11.1.0");Q13=makeQuery(id+"F6.opPattern","COPY",BODY,{"derivedFrom":makeQuery(id+"F3.opLoft","SWEPT_BODY",BODY,{"disambiguationData":[OSD([makeQuery(id+"F0.imprint","IMPRINT",FACE,{"disambiguationData":[TD([[makeQuery(id+"F0.imprint","IMPRINT",EDGE,{"derivedFrom":subQ1}),1.0]])]}),makeQuery(id+"F2.imprint","IMPRINT",FACE,{"disambiguationData":[TD([[makeQuery(id+"F2.imprint","IMPRINT",EDGE,{"derivedFrom":sQuery(id+"F2.wireOp",EDGE,"E14.0.0")}),1.0]])]})])]}),"instanceName":"11"});}
            var Q14;
            {var subQ1=sQuery(id+"F0.wireOp",EDGE,"E11.1.0");Q14=makeQuery(id+"F6.opPattern","COPY",BODY,{"derivedFrom":makeQuery(id+"F3.opLoft","SWEPT_BODY",BODY,{"disambiguationData":[OSD([makeQuery(id+"F0.imprint","IMPRINT",FACE,{"disambiguationData":[TD([[makeQuery(id+"F0.imprint","IMPRINT",EDGE,{"derivedFrom":subQ1}),1.0]])]}),makeQuery(id+"F2.imprint","IMPRINT",FACE,{"disambiguationData":[TD([[makeQuery(id+"F2.imprint","IMPRINT",EDGE,{"derivedFrom":sQuery(id+"F2.wireOp",EDGE,"E14.0.0")}),1.0]])]})])]}),"instanceName":"10"});}
            var Q15;
            {var subQ1=sQuery(id+"F0.wireOp",EDGE,"E11.1.0");Q15=makeQuery(id+"F6.opPattern","COPY",BODY,{"derivedFrom":makeQuery(id+"F3.opLoft","SWEPT_BODY",BODY,{"disambiguationData":[OSD([makeQuery(id+"F0.imprint","IMPRINT",FACE,{"disambiguationData":[TD([[makeQuery(id+"F0.imprint","IMPRINT",EDGE,{"derivedFrom":subQ1}),1.0]])]}),makeQuery(id+"F2.imprint","IMPRINT",FACE,{"disambiguationData":[TD([[makeQuery(id+"F2.imprint","IMPRINT",EDGE,{"derivedFrom":sQuery(id+"F2.wireOp",EDGE,"E14.0.0")}),1.0]])]})])]}),"instanceName":"9"});}
            var Q16;
            {var subQ1=sQuery(id+"F0.wireOp",EDGE,"E11.1.0");Q16=makeQuery(id+"F6.opPattern","COPY",BODY,{"derivedFrom":makeQuery(id+"F3.opLoft","SWEPT_BODY",BODY,{"disambiguationData":[OSD([makeQuery(id+"F0.imprint","IMPRINT",FACE,{"disambiguationData":[TD([[makeQuery(id+"F0.imprint","IMPRINT",EDGE,{"derivedFrom":subQ1}),1.0]])]}),makeQuery(id+"F2.imprint","IMPRINT",FACE,{"disambiguationData":[TD([[makeQuery(id+"F2.imprint","IMPRINT",EDGE,{"derivedFrom":sQuery(id+"F2.wireOp",EDGE,"E14.0.0")}),1.0]])]})])]}),"instanceName":"8"});}
            var Q17;
            {var subQ1=sQuery(id+"F0.wireOp",EDGE,"E11.1.0");Q17=makeQuery(id+"F6.opPattern","COPY",BODY,{"derivedFrom":makeQuery(id+"F3.opLoft","SWEPT_BODY",BODY,{"disambiguationData":[OSD([makeQuery(id+"F0.imprint","IMPRINT",FACE,{"disambiguationData":[TD([[makeQuery(id+"F0.imprint","IMPRINT",EDGE,{"derivedFrom":subQ1}),1.0]])]}),makeQuery(id+"F2.imprint","IMPRINT",FACE,{"disambiguationData":[TD([[makeQuery(id+"F2.imprint","IMPRINT",EDGE,{"derivedFrom":sQuery(id+"F2.wireOp",EDGE,"E14.0.0")}),1.0]])]})])]}),"instanceName":"7"});}
            var Q18;
            {var subQ1=sQuery(id+"F0.wireOp",EDGE,"E11.1.0");Q18=makeQuery(id+"F6.opPattern","COPY",BODY,{"derivedFrom":makeQuery(id+"F3.opLoft","SWEPT_BODY",BODY,{"disambiguationData":[OSD([makeQuery(id+"F0.imprint","IMPRINT",FACE,{"disambiguationData":[TD([[makeQuery(id+"F0.imprint","IMPRINT",EDGE,{"derivedFrom":subQ1}),1.0]])]}),makeQuery(id+"F2.imprint","IMPRINT",FACE,{"disambiguationData":[TD([[makeQuery(id+"F2.imprint","IMPRINT",EDGE,{"derivedFrom":sQuery(id+"F2.wireOp",EDGE,"E14.0.0")}),1.0]])]})])]}),"instanceName":"6"});}
            var Q19;
            {var subQ1=sQuery(id+"F0.wireOp",EDGE,"E11.1.0");Q19=makeQuery(id+"F6.opPattern","COPY",BODY,{"derivedFrom":makeQuery(id+"F3.opLoft","SWEPT_BODY",BODY,{"disambiguationData":[OSD([makeQuery(id+"F0.imprint","IMPRINT",FACE,{"disambiguationData":[TD([[makeQuery(id+"F0.imprint","IMPRINT",EDGE,{"derivedFrom":subQ1}),1.0]])]}),makeQuery(id+"F2.imprint","IMPRINT",FACE,{"disambiguationData":[TD([[makeQuery(id+"F2.imprint","IMPRINT",EDGE,{"derivedFrom":sQuery(id+"F2.wireOp",EDGE,"E14.0.0")}),1.0]])]})])]}),"instanceName":"5"});}
            var Q20;
            {var subQ1=sQuery(id+"F0.wireOp",EDGE,"E11.1.0");Q20=makeQuery(id+"F6.opPattern","COPY",BODY,{"derivedFrom":makeQuery(id+"F3.opLoft","SWEPT_BODY",BODY,{"disambiguationData":[OSD([makeQuery(id+"F0.imprint","IMPRINT",FACE,{"disambiguationData":[TD([[makeQuery(id+"F0.imprint","IMPRINT",EDGE,{"derivedFrom":subQ1}),1.0]])]}),makeQuery(id+"F2.imprint","IMPRINT",FACE,{"disambiguationData":[TD([[makeQuery(id+"F2.imprint","IMPRINT",EDGE,{"derivedFrom":sQuery(id+"F2.wireOp",EDGE,"E14.0.0")}),1.0]])]})])]}),"instanceName":"4"});}
            var Q21;
            {var subQ1=sQuery(id+"F0.wireOp",EDGE,"E11.1.0");Q21=makeQuery(id+"F6.opPattern","COPY",BODY,{"derivedFrom":makeQuery(id+"F3.opLoft","SWEPT_BODY",BODY,{"disambiguationData":[OSD([makeQuery(id+"F0.imprint","IMPRINT",FACE,{"disambiguationData":[TD([[makeQuery(id+"F0.imprint","IMPRINT",EDGE,{"derivedFrom":subQ1}),1.0]])]}),makeQuery(id+"F2.imprint","IMPRINT",FACE,{"disambiguationData":[TD([[makeQuery(id+"F2.imprint","IMPRINT",EDGE,{"derivedFrom":sQuery(id+"F2.wireOp",EDGE,"E14.0.0")}),1.0]])]})])]}),"instanceName":"3"});}
            var Q22;
            {var subQ1=sQuery(id+"F0.wireOp",EDGE,"E11.1.0");Q22=makeQuery(id+"F6.opPattern","COPY",BODY,{"derivedFrom":makeQuery(id+"F3.opLoft","SWEPT_BODY",BODY,{"disambiguationData":[OSD([makeQuery(id+"F0.imprint","IMPRINT",FACE,{"disambiguationData":[TD([[makeQuery(id+"F0.imprint","IMPRINT",EDGE,{"derivedFrom":subQ1}),1.0]])]}),makeQuery(id+"F2.imprint","IMPRINT",FACE,{"disambiguationData":[TD([[makeQuery(id+"F2.imprint","IMPRINT",EDGE,{"derivedFrom":sQuery(id+"F2.wireOp",EDGE,"E14.0.0")}),1.0]])]})])]}),"instanceName":"2"});}
            var Q23;
            {var subQ1=sQuery(id+"F0.wireOp",EDGE,"E11.1.0");Q23=makeQuery(id+"F6.opPattern","COPY",BODY,{"derivedFrom":makeQuery(id+"F3.opLoft","SWEPT_BODY",BODY,{"disambiguationData":[OSD([makeQuery(id+"F0.imprint","IMPRINT",FACE,{"disambiguationData":[TD([[makeQuery(id+"F0.imprint","IMPRINT",EDGE,{"derivedFrom":subQ1}),1.0]])]}),makeQuery(id+"F2.imprint","IMPRINT",FACE,{"disambiguationData":[TD([[makeQuery(id+"F2.imprint","IMPRINT",EDGE,{"derivedFrom":sQuery(id+"F2.wireOp",EDGE,"E14.0.0")}),1.0]])]})])]}),"instanceName":"1"});}
            booleanBodies(context, id + "F7", {"operationType" : BooleanOperationType.UNION, "tools" : qUnion([Q0, Q1, Q2, Q3, Q4, Q5, Q6, Q7, Q8, Q9, Q10, Q11, Q12, Q13, Q14, Q15, Q16, Q17, Q18, Q19, Q20, Q21, Q22, Q23])});
        }
        {
            var Q0;
            {var subQ0=makeQuery(id+"F5.boolean.opBoolean","MERGE",FACE,{"derivedFrom":[makeQuery(id+"F3.opLoft","CAP_FACE",FACE,{"disambiguationData":[OSD([makeQuery(id+"F2.imprint","IMPRINT",FACE,{"disambiguationData":[TD([[makeQuery(id+"F2.imprint","IMPRINT",EDGE,{"derivedFrom":sQuery(id+"F2.wireOp",EDGE,"E14.0.0")}),1.0]])]})])],"isStart":true}),makeQuery(id+"F5.opExtrude","CAP_FACE",FACE,{"disambiguationData":[OSD([sQuery(id+"F4.wireOp",EDGE,"E15")])],"isStart":true})]});Q0=makeQuery(id+"F7.opBoolean","MERGE",FACE,{"derivedFrom":[subQ0,makeQuery(id+"F6.opPattern","COPY",FACE,{"derivedFrom":subQ0,"instanceName":"1"}),makeQuery(id+"F6.opPattern","COPY",FACE,{"derivedFrom":subQ0,"instanceName":"2"}),makeQuery(id+"F6.opPattern","COPY",FACE,{"derivedFrom":subQ0,"instanceName":"3"}),makeQuery(id+"F6.opPattern","COPY",FACE,{"derivedFrom":subQ0,"instanceName":"4"}),makeQuery(id+"F6.opPattern","COPY",FACE,{"derivedFrom":subQ0,"instanceName":"5"}),makeQuery(id+"F6.opPattern","COPY",FACE,{"derivedFrom":subQ0,"instanceName":"6"}),makeQuery(id+"F6.opPattern","COPY",FACE,{"derivedFrom":subQ0,"instanceName":"7"}),makeQuery(id+"F6.opPattern","COPY",FACE,{"derivedFrom":subQ0,"instanceName":"8"}),makeQuery(id+"F6.opPattern","COPY",FACE,{"derivedFrom":subQ0,"instanceName":"9"}),makeQuery(id+"F6.opPattern","COPY",FACE,{"derivedFrom":subQ0,"instanceName":"10"}),makeQuery(id+"F6.opPattern","COPY",FACE,{"derivedFrom":subQ0,"instanceName":"11"}),makeQuery(id+"F6.opPattern","COPY",FACE,{"derivedFrom":subQ0,"instanceName":"12"}),makeQuery(id+"F6.opPattern","COPY",FACE,{"derivedFrom":subQ0,"instanceName":"13"}),makeQuery(id+"F6.opPattern","COPY",FACE,{"derivedFrom":subQ0,"instanceName":"14"}),makeQuery(id+"F6.opPattern","COPY",FACE,{"derivedFrom":subQ0,"instanceName":"15"}),makeQuery(id+"F6.opPattern","COPY",FACE,{"derivedFrom":subQ0,"instanceName":"16"}),makeQuery(id+"F6.opPattern","COPY",FACE,{"derivedFrom":subQ0,"instanceName":"17"}),makeQuery(id+"F6.opPattern","COPY",FACE,{"derivedFrom":subQ0,"instanceName":"18"}),makeQuery(id+"F6.opPattern","COPY",FACE,{"derivedFrom":subQ0,"instanceName":"19"}),makeQuery(id+"F6.opPattern","COPY",FACE,{"derivedFrom":subQ0,"instanceName":"20"}),makeQuery(id+"F6.opPattern","COPY",FACE,{"derivedFrom":subQ0,"instanceName":"21"}),makeQuery(id+"F6.opPattern","COPY",FACE,{"derivedFrom":subQ0,"instanceName":"22"}),makeQuery(id+"F6.opPattern","COPY",FACE,{"derivedFrom":subQ0,"instanceName":"23"})]});}
            var sketch = newSketch(context, id + "F8", { "sketchPlane" : qUnion([Q0])});
            skCircle(sketch, "E16", {"center": v(0, 0) * mm, "radius": 6.35 * mm});
            skSolve(sketch);
        }
        {
            var Q0;
            Q0 = qSketchRegion(id + "F8", true);
            extrude(context, id + "F9", {"entities" : qUnion([Q0]), "operationType" : NewBodyOperationType.REMOVE, "endBound" : BoundingType.THROUGH_ALL, "oppositeDirection" : true, "depth" : 25.4 * mm});
        }
    });
